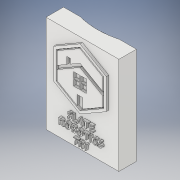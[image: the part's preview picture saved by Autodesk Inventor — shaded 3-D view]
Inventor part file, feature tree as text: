
AUTODESK INVENTOR PART (.ipt)
format: ipt  version: 2017 SP1 (Build 210196100, 196)  size: 1,041,408 bytes
history: native  units: in
note: dims shown in document units (in); Inventor stores cm internally (conversion verified against a paired STEP export)
features: projected_geometry x20, extrude x4, sketch x4, other x3
ambient origin geometry x8: Origin, YZ Plane, XZ Plane, XY Plane, X Axis, Y Axis, Z Axis, Center Point
bodies: Solid2 (feature_tree)
feature tree (31):
  other  "BP002b.ipt"
  extrude  "Extrusion3"  Depth=0.2638in TaperAngle=0.0deg
  extrude  "Extrusion4"  Depth=0.6299in
  extrude  "Extrusion5"  Depth=0.2638in TaperAngle=0.0deg
  extrude  "Extrusion7"  [1 undecoded]
  other  "Solid1::BP002b.ipt"
  other  "TaggingFeature1"
  sketch  "Sketch4"  dims[d62=0.0394in d63=0.2638in d64=0.0in]
  projected_geometry  "Projected Loop1"
  sketch  "Sketch5"  dims[d65=0.2835in d66=0.0in d67=0.6299in]
  sketch  "Sketch6"  dims[d68=1.2169in d69=0.2638in d70=0.0in]
  sketch  "Sketch9"  dims[d74=0.0315in d75=0.0in]
  projected_geometry  "Projected Loop5"
  projected_geometry  "Projected Loop6"
  projected_geometry  "Projected Loop7"
  projected_geometry  "Projected Loop8"
  projected_geometry  "Projected Loop9"
  projected_geometry  "Projected Loop10"
  projected_geometry  "Projected Loop11"
  projected_geometry  "Projected Loop12"
  projected_geometry  "Projected Loop13"
  projected_geometry  "Projected Loop14"
  projected_geometry  "Projected Loop15"
  projected_geometry  "Projected Loop16"
  projected_geometry  "Projected Loop17"
  projected_geometry  "Projected Loop18"
  projected_geometry  "Projected Loop19"
  projected_geometry  "Projected Loop20"
  projected_geometry  "Projected Loop21"
  projected_geometry  "Projected Loop22"
  projected_geometry  "Projected Loop23"
note: 1 required parameter value undecoded (feature->parameter linkage not recoverable at this tier; creation-order binding heuristic only, values carry confidence <= 0.55)
